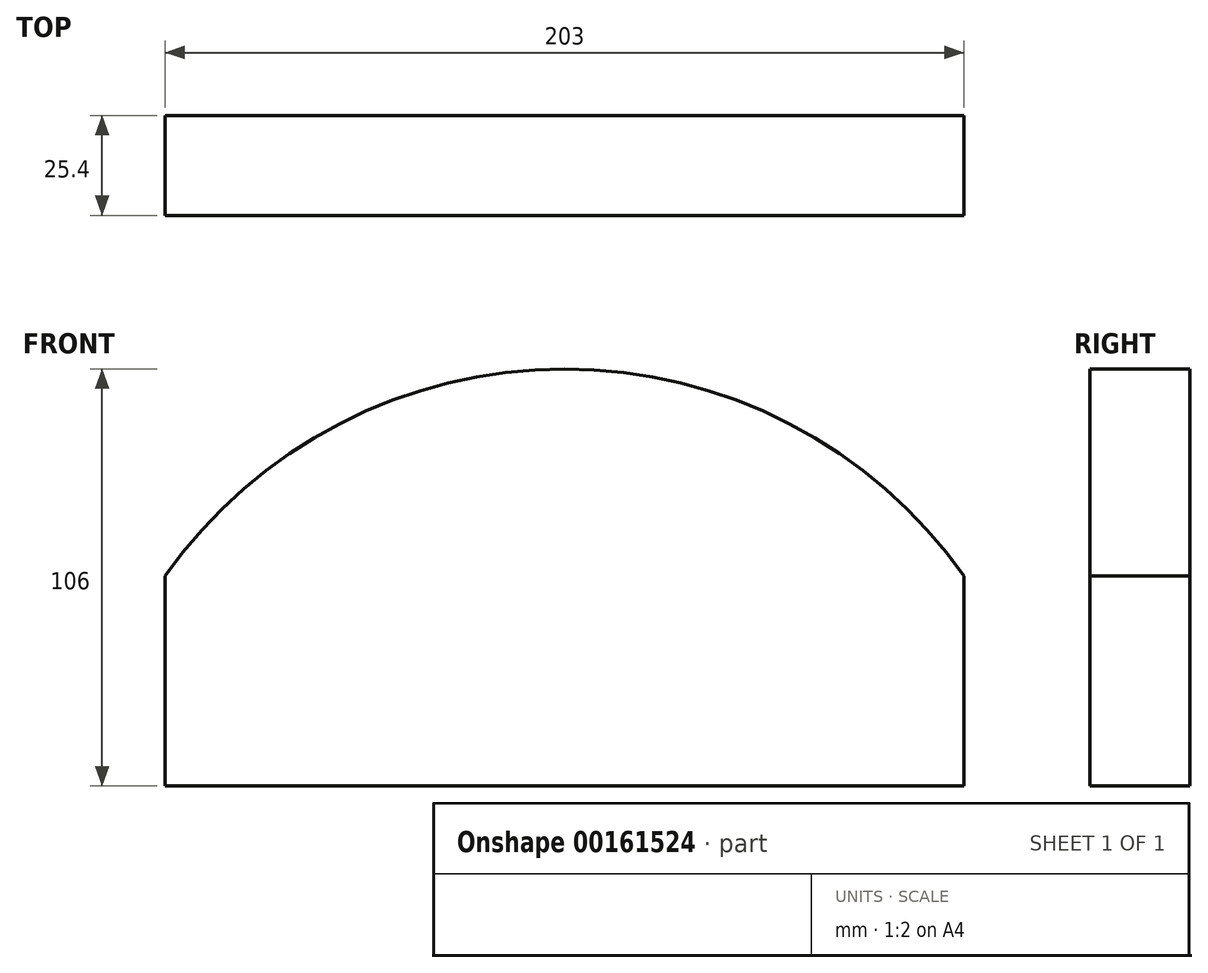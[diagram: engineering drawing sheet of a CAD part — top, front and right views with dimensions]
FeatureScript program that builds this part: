
annotation { "Feature Type Name" : "Feature", "Feature Type Description" : "" }
export const myFeature = defineFeature(function(context is Context, id is Id, definition is map)
    precondition{}
    {
        {
            var Q0;
            Q0=qCreatedBy(makeId("Front.planeOp"),FACE);
            var sketch = newSketch(context, id + "F0", { "sketchPlane" : qUnion([Q0])});
            skLineSegment(sketch, "E0", {"start": v(-101.5, 53.34) * mm, "end": v(-101.5, 0) * mm});
            skLineSegment(sketch, "E1", {"start": v(-101.5, 0) * mm, "end": v(101.5, 0) * mm});
            skLineSegment(sketch, "E2", {"start": v(101.5, 0) * mm, "end": v(101.5, 53.34) * mm});
            skArc(sketch, "E3", {"start": v(101.5, 53.34) * mm, "mid": v(0, 106) * mm, "end": v(-101.5, 53.34) * mm});
            skSolve(sketch);
        }
        {
            var Q0;
            Q0 = qSketchRegion(id + "F0", true);
            extrude(context, id + "F1", {"entities" : qUnion([Q0]), "depth" : 25.4 * mm});
        }
    });
